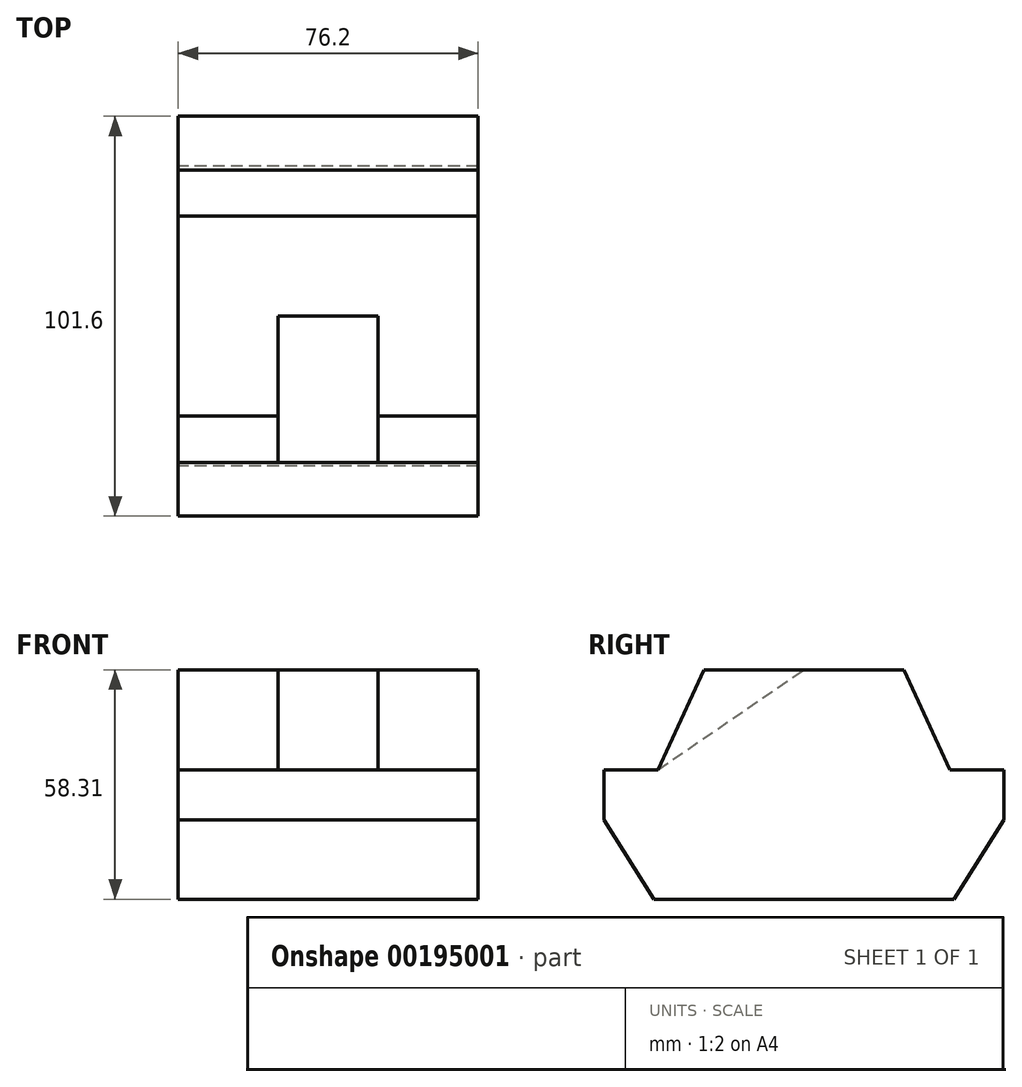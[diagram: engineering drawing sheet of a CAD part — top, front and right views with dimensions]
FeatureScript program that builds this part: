
annotation { "Feature Type Name" : "Feature", "Feature Type Description" : "" }
export const myFeature = defineFeature(function(context is Context, id is Id, definition is map)
    precondition{}
    {
        {
            var Q0;
            Q0=qCreatedBy(makeId("Right.planeOp"),FACE);
            var sketch = newSketch(context, id + "F0", { "sketchPlane" : qUnion([Q0])});
            skLineSegment(sketch, "E0", {"start": v(0, 0) * mm, "end": v(0, 58.3) * mm});
            skLineSegment(sketch, "E1", {"start": v(0, 0) * mm, "end": v(-38.1, 0) * mm});
            skLineSegment(sketch, "E2", {"start": v(-25.4, 58.3) * mm, "end": v(0, 58.3) * mm});
            skLineSegment(sketch, "E3", {"start": v(-25.4, 58.3) * mm, "end": v(-37.1, 32.9) * mm});
            skLineSegment(sketch, "E4", {"start": v(-37.1, 32.9) * mm, "end": v(-50.8, 32.9) * mm});
            skLineSegment(sketch, "E5", {"start": v(-50.8, 32.9) * mm, "end": v(-50.8, 20.2) * mm});
            skLineSegment(sketch, "E6", {"start": v(-50.8, 20.2) * mm, "end": v(-38.1, 0) * mm});
            skLineSegment(sketch, "E7", {"start": v(0, 75.06) * mm, "end": v(0, -1.74) * mm, "construction": true});
            skLineSegment(sketch, "E8.MirrorCS", {"start": v(50.8, 20.2) * mm, "end": v(38.1, 0) * mm});
            skLineSegment(sketch, "E9.MirrorCS", {"start": v(50.8, 32.9) * mm, "end": v(50.8, 20.2) * mm});
            skLineSegment(sketch, "E10.MirrorCS", {"start": v(37.1, 32.9) * mm, "end": v(50.8, 32.9) * mm});
            skLineSegment(sketch, "E11.MirrorCS", {"start": v(25.4, 58.3) * mm, "end": v(37.1, 32.9) * mm});
            skLineSegment(sketch, "E12.MirrorCS", {"start": v(25.4, 58.3) * mm, "end": v(0, 58.3) * mm});
            skLineSegment(sketch, "E13.MirrorCS", {"start": v(0, 0) * mm, "end": v(38.1, 0) * mm});
            skSolve(sketch);
        }
        {
            var Q0;
            Q0 = qSketchRegion(id + "F0", true);
            extrude(context, id + "F1", {"entities" : qUnion([Q0]), "depth" : 76.2 * mm});
        }
        {
            var Q0;
            Q0=makeQuery(id+"F1.opExtrude","CAP_FACE",FACE,{"disambiguationData":[OSD([sQuery(id+"F0.wireOp",EDGE,"E0"),sQuery(id+"F0.wireOp",EDGE,"E1"),sQuery(id+"F0.wireOp",EDGE,"E2"),sQuery(id+"F0.wireOp",EDGE,"E3"),sQuery(id+"F0.wireOp",EDGE,"E4"),sQuery(id+"F0.wireOp",EDGE,"E5"),sQuery(id+"F0.wireOp",EDGE,"E6")])],"isStart":false});
            var Q1;
            Q1=makeQuery(id+"F1.opExtrude","CAP_FACE",FACE,{"disambiguationData":[OSD([sQuery(id+"F0.wireOp",EDGE,"E0"),sQuery(id+"F0.wireOp",EDGE,"E1"),sQuery(id+"F0.wireOp",EDGE,"E2"),sQuery(id+"F0.wireOp",EDGE,"E3"),sQuery(id+"F0.wireOp",EDGE,"E4"),sQuery(id+"F0.wireOp",EDGE,"E5"),sQuery(id+"F0.wireOp",EDGE,"E6")])],"isStart":true});
            cPlane(context, id + "F2", {"entities" : qUnion([Q0, Q1]), "cplaneType" : CPlaneType.MID_PLANE, "offset" : 25.4 * mm, "width" : 152.4 * mm, "height" : 152.4 * mm});
        }
        {
            var Q0;
            Q0=qCreatedBy(id+"F2.planeOp",FACE);
            var sketch = newSketch(context, id + "F3", { "sketchPlane" : qUnion([Q0])});
            skLineSegment(sketch, "E14", {"start": v(-25.4, 58.3) * mm, "end": v(0, 58.3) * mm});
            skLineSegment(sketch, "E15", {"start": v(-25.4, 58.3) * mm, "end": v(-37.1, 32.9) * mm});
            skLineSegment(sketch, "E16", {"start": v(-37.1, 32.9) * mm, "end": v(0, 58.3) * mm});
            skSolve(sketch);
        }
        {
            var Q0;
            Q0 = qSketchRegion(id + "F3", true);
            extrude(context, id + "F4", {"entities" : qUnion([Q0]), "operationType" : NewBodyOperationType.REMOVE, "oppositeDirection" : true, "depth" : 12.7 * mm, "hasSecondDirection" : true, "secondDirectionOppositeDirection" : false, "secondDirectionDepth" : 12.7 * mm});
        }
    });
